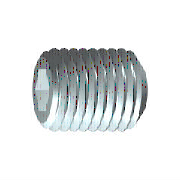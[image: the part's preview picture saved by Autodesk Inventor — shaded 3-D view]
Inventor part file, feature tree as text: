
AUTODESK INVENTOR PART (.ipt)
format: ipt  version: 2023.3 (Build 273359000, 359)  size: 166,400 bytes
history: native  units: mm (DEFAULTED — no unit token found)
features: other x2, sketch x2, extrude x1, plane x1
ambient origin geometry x8: Origin, YZ Plane, XZ Plane, XY Plane, X Axis, Y Axis, Z Axis, Center Point
bodies: Solid1 (feature_tree)
feature tree (6):
  other  "Körper"
  extrude  "Loch"  TaperAngle=60.0deg  [1 undecoded]
  other  "Work Axis1"
  plane  "Work Plane1"
  sketch  "Skizze1"  dims[d0=1.2mm d1=60.0deg]
  sketch  "Skizze2"  dims[d2=3.0mm d3=1.732051mm d6=90.0deg d4=0.0mm d5=3.0mm d7=0.306725mm d8=60.0deg d21=10.0mm d9=0.0mm d11=3.0mm d12=0.0mm d13=0.306725mm d14=60.0deg d15=0.0mm d29=0.306725mm d30=0.306725mm d31=0.0mm]
note: 1 required parameter value undecoded (feature->parameter linkage not recoverable at this tier; creation-order binding heuristic only, values carry confidence <= 0.55)
